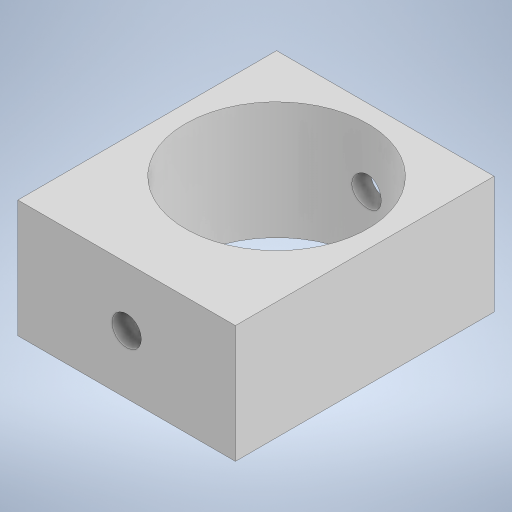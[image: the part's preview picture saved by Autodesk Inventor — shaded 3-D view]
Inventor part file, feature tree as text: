
AUTODESK INVENTOR PART (.ipt)
format: ipt  version: 2023.5 (Build 275446000, 446)  size: 233,984 bytes
history: native  units: in
note: dims shown in document units (in); Inventor stores cm internally (conversion verified against a paired STEP export)
features: extrude x5, sketch x3
ambient origin geometry x8: Origin, YZ Plane, XZ Plane, XY Plane, X Axis, Y Axis, Z Axis, Center Point
bodies: Solid1 (feature_tree)
feature tree (8):
  extrude  "Extrusion1"  Depth=1.4567in
  extrude  "Extrusion2"  Depth=0.7283in
  extrude  "Extrusion3"  Depth=0.1969in TaperAngle=0.0deg
  extrude  "Extrusion4"  Depth=0.1969in
  extrude  "Extrusion5"  Depth=0.1969in TaperAngle=0.0deg
  sketch  "Sketch3"  dims[d0=1.4567in d1=1.4567in]
  sketch  "Sketch5"  dims[d2=0.7283in d3=0.7283in]
  sketch  "Sketch6"  dims[d4=1.2205in d5=0.7874in d6=0.0in d8=0.3543in d9=0.1969in d10=0.0in d11=0.1969in d12=0.1969in d13=0.0in d14=0.0787in d15=0.0in d16=0.1969in d17=0.0in d18=0.7283in d19=0.7283in d20=0.7283in]
